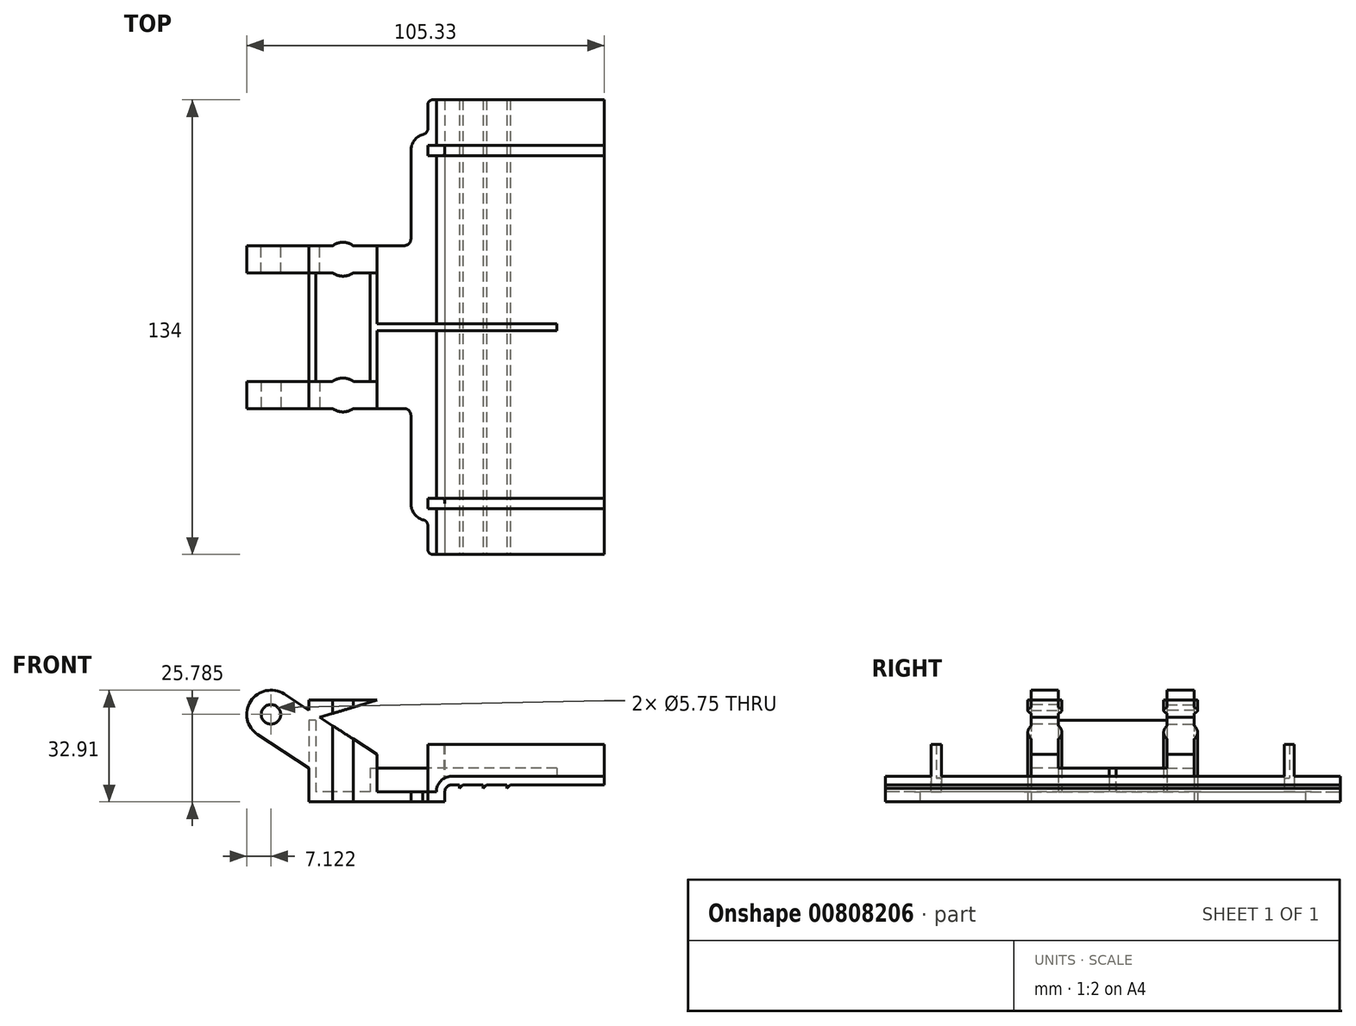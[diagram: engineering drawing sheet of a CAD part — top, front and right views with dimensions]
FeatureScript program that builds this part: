
annotation { "Feature Type Name" : "Feature", "Feature Type Description" : "" }
export const myFeature = defineFeature(function(context is Context, id is Id, definition is map)
    precondition{}
    {
        {
            var Q0;
            Q0=qCreatedBy(makeId("Top.planeOp"),FACE);
            var sketch = newSketch(context, id + "F0", { "sketchPlane" : qUnion([Q0])});
            skLineSegment(sketch, "E0", {"start": v(0, 0) * mm, "end": v(55, 0) * mm});
            skLineSegment(sketch, "E1", {"start": v(55, 0) * mm, "end": v(55, -1) * mm});
            skLineSegment(sketch, "E2", {"start": v(55, -1) * mm, "end": v(2, -1) * mm});
            skLineSegment(sketch, "E3", {"start": v(0, -1) * mm, "end": v(0, 0) * mm});
            skLineSegment(sketch, "E4", {"start": v(0, 0) * mm, "end": v(0, -16) * mm});
            skLineSegment(sketch, "E5", {"start": v(2, -24) * mm, "end": v(2, -1) * mm});
            skLineSegment(sketch, "E6", {"start": v(2, 0) * mm, "end": v(0, 0) * mm});
            skLineSegment(sketch, "E7.bottom", {"start": v(2, -24) * mm, "end": v(-5, -24) * mm});
            skLineSegment(sketch, "E7.top", {"start": v(0, -16) * mm, "end": v(-5, -16) * mm});
            skLineSegment(sketch, "E7.left", {"start": v(2, -24) * mm, "end": v(2, -16) * mm});
            skLineSegment(sketch, "E7.right", {"start": v(-18, -24) * mm, "end": v(-18, -16) * mm});
            skLineSegment(sketch, "E8", {"start": v(-18, -16) * mm, "end": v(-18, 0) * mm});
            skLineSegment(sketch, "E9", {"start": v(-18, 0) * mm, "end": v(-16, 0) * mm});
            skLineSegment(sketch, "E10", {"start": v(-16, 0) * mm, "end": v(-16, -16) * mm});
            skCircle(sketch, "E11", {"center": v(-8, -20) * mm, "radius": 5 * mm});
            skLineSegment(sketch, "E12", {"start": v(-16, 0) * mm, "end": v(0, 0) * mm});
            skLineSegment(sketch, "E13", {"start": v(2, -24) * mm, "end": v(10, -24) * mm});
            skLineSegment(sketch, "E14", {"start": v(12, -26) * mm, "end": v(12, -52) * mm});
            skLineSegment(sketch, "E15", {"start": v(17, -57) * mm, "end": v(22, -57) * mm});
            skLineSegment(sketch, "E16", {"start": v(22, -57) * mm, "end": v(22, -1) * mm});
            skLineSegment(sketch, "E17", {"start": v(0, -16) * mm, "end": v(2, -16) * mm});
            skCircle(sketch, "E18", {"center": v(17, -52) * mm, "radius": 5 * mm});
            skPoint(sketch, "E19.visualSharp", {"position": v(12, -57) * mm});
            skArc(sketch, "E19.filletArc", {"start": v(12, -52) * mm, "mid": v(13.46, -55.54) * mm, "end": v(17, -57) * mm});
            skLineSegment(sketch, "E20", {"start": v(2, -20) * mm, "end": v(-18, -20) * mm, "construction": true});
            skLineSegment(sketch, "E21.trimOffspring", {"start": v(-11, -16) * mm, "end": v(-18, -16) * mm});
            skLineSegment(sketch, "E22.trimOffspring", {"start": v(-11, -24) * mm, "end": v(-18, -24) * mm});
            skLineSegment(sketch, "E23.bottom", {"start": v(17, -53.5) * mm, "end": v(69, -53.5) * mm});
            skLineSegment(sketch, "E23.top", {"start": v(17, -50.5) * mm, "end": v(69, -50.5) * mm});
            skLineSegment(sketch, "E23.left", {"start": v(17, -53.5) * mm, "end": v(17, -50.5) * mm});
            skLineSegment(sketch, "E23.right", {"start": v(69, -53.5) * mm, "end": v(69, -50.5) * mm});
            skLineSegment(sketch, "E24", {"start": v(17, -52) * mm, "end": v(69, -52) * mm, "construction": true});
            skLineSegment(sketch, "E25.top", {"start": v(18.5, -67) * mm, "end": v(22, -67) * mm});
            skLineSegment(sketch, "E25.left", {"start": v(17, -58.5) * mm, "end": v(17, -65.5) * mm});
            skLineSegment(sketch, "E25.right", {"start": v(22, -57) * mm, "end": v(22, -67) * mm});
            skPoint(sketch, "E26.visualSharp", {"position": v(17, -67) * mm});
            skArc(sketch, "E26.filletArc", {"start": v(17, -65.5) * mm, "mid": v(17.44, -66.56) * mm, "end": v(18.5, -67) * mm});
            skPoint(sketch, "E27.visualSharp", {"position": v(12, -24) * mm});
            skArc(sketch, "E27.filletArc", {"start": v(12, -26) * mm, "mid": v(11.41, -24.59) * mm, "end": v(10, -24) * mm});
            skArc(sketch, "E28", {"start": v(17, -58.5) * mm, "mid": v(16.57, -57.36) * mm, "end": v(15.5, -56.77) * mm});
            skSolve(sketch);
        }
        {
            var Q0;
            Q0=makeQuery(id+"F0.imprint","IMPRINT",FACE,{"disambiguationData":[TD([[makeQuery(id+"F0.imprint","IMPRINT",EDGE,{"derivedFrom":sQuery(id+"F0.wireOp",EDGE,"E0")}),-1.0]])]});
            extrude(context, id + "F1", {"entities" : qUnion([Q0]), "depth" : 10 * mm, "offsetDistance" : 25 * mm});
        }
        {
            var Q0;
            {var subQ2=sQuery(id+"F0.wireOp",EDGE,"E7.bottom");Q0=makeQuery(id+"F0.imprint","IMPRINT",FACE,{"disambiguationData":[TD([[makeQuery(id+"F0.imprint","IMPRINT",EDGE,{"derivedFrom":subQ2}),-1.0]])]});}
            var Q1;
            {var subQ0=sQuery(id+"F0.wireOp",EDGE,"E11");var subQ1=makeQuery(id+"F0.imprint","INTERSECT",VERTEX,{"derivedFrom":[sQuery(id+"F0.wireOp",EDGE,"E7.top"),subQ0]});Q1=makeQuery(id+"F0.imprint","IMPRINT",FACE,{"disambiguationData":[TD([[makeQuery(id+"F0.imprint","IMPRINT",EDGE,{"disambiguationData":[TD([[subQ1,-1.0]])],"derivedFrom":subQ0}),1.0]])]});}
            var Q2;
            {var subQ1=sQuery(id+"F0.wireOp",EDGE,"E7.right");Q2=makeQuery(id+"F0.imprint","IMPRINT",FACE,{"disambiguationData":[TD([[makeQuery(id+"F0.imprint","IMPRINT",EDGE,{"derivedFrom":subQ1}),-1.0]])]});}
            extrude(context, id + "F2", {"entities" : qUnion([Q0, Q1, Q2]), "depth" : 30 * mm, "offsetDistance" : 25 * mm});
        }
        {
            var Q0;
            {var subQ0=sQuery(id+"F0.wireOp",EDGE,"E7.top");Q0=makeQuery(id+"F0.imprint","IMPRINT",FACE,{"disambiguationData":[TD([[makeQuery(id+"F0.imprint","IMPRINT",EDGE,{"derivedFrom":subQ0}),-1.0]])]});}
            var Q1;
            {var subQ1=sQuery(id+"F0.wireOp",EDGE,"E5");Q1=makeQuery(id+"F0.imprint","IMPRINT",FACE,{"disambiguationData":[TD([[makeQuery(id+"F0.imprint","IMPRINT",EDGE,{"derivedFrom":subQ1}),-1.0]])]});}
            var Q2;
            {var subQ0=sQuery(id+"F0.wireOp",EDGE,"E15");Q2=makeQuery(id+"F0.imprint","IMPRINT",FACE,{"disambiguationData":[TD([[makeQuery(id+"F0.imprint","IMPRINT",EDGE,{"derivedFrom":subQ0}),1.0]])]});}
            var Q3;
            Q3=makeQuery(id+"F0.imprint","IMPRINT",FACE,{"disambiguationData":[TD([[makeQuery(id+"F0.imprint","IMPRINT",EDGE,{"derivedFrom":sQuery(id+"F0.wireOp",EDGE,"E15")}),-1.0]])]});
            var Q4;
            {var subQ0=sQuery(id+"F0.wireOp",EDGE,"E23.left");Q4=makeQuery(id+"F0.imprint","IMPRINT",FACE,{"disambiguationData":[TD([[makeQuery(id+"F0.imprint","IMPRINT",EDGE,{"derivedFrom":subQ0}),-1.0]])]});}
            var Q5;
            {var subQ0=sQuery(id+"F0.wireOp",EDGE,"E23.left");Q5=makeQuery(id+"F0.imprint","IMPRINT",FACE,{"disambiguationData":[TD([[makeQuery(id+"F0.imprint","IMPRINT",EDGE,{"derivedFrom":subQ0}),1.0]])]});}
            var Q6;
            {var subQ0=sQuery(id+"F0.wireOp",EDGE,"E23.top");var subQ1=sQuery(id+"F0.wireOp",EDGE,"E16");var subQ2=makeQuery(id+"F0.imprint","INTERSECT",VERTEX,{"derivedFrom":[subQ1,subQ0]});Q6=makeQuery(id+"F0.imprint","IMPRINT",FACE,{"disambiguationData":[TD([[makeQuery(id+"F0.imprint","IMPRINT",EDGE,{"disambiguationData":[TD([[subQ2,1.0]])],"derivedFrom":subQ1}),1.0]])]});}
            var Q7;
            {var subQ0=sQuery(id+"F0.wireOp",EDGE,"E23.bottom");var subQ1=sQuery(id+"F0.wireOp",EDGE,"E16");var subQ2=makeQuery(id+"F0.imprint","INTERSECT",VERTEX,{"derivedFrom":[subQ1,subQ0]});Q7=makeQuery(id+"F0.imprint","IMPRINT",FACE,{"disambiguationData":[TD([[makeQuery(id+"F0.imprint","IMPRINT",EDGE,{"disambiguationData":[TD([[subQ2,-1.0]])],"derivedFrom":subQ1}),1.0]])]});}
            extrude(context, id + "F3", {"entities" : qUnion([Q0, Q1, Q2, Q3, Q4, Q5, Q6, Q7]), "depth" : 3 * mm, "offsetDistance" : 25 * mm});
        }
        {
            var Q0;
            {var subQ0=sQuery(id+"F0.wireOp",EDGE,"E18");var subQ1=makeQuery(id+"F0.imprint","INTERSECT",VERTEX,{"derivedFrom":[sQuery(id+"F0.wireOp",EDGE,"E14"),subQ0]});Q0=makeQuery(id+"F0.imprint","IMPRINT",FACE,{"disambiguationData":[TD([[makeQuery(id+"F0.imprint","IMPRINT",EDGE,{"disambiguationData":[TD([[subQ1,-1.0]])],"derivedFrom":subQ0}),1.0]])]});}
            var Q1;
            {var subQ0=sQuery(id+"F0.wireOp",EDGE,"E23.bottom");var subQ1=sQuery(id+"F0.wireOp",EDGE,"E16");var subQ2=makeQuery(id+"F0.imprint","INTERSECT",VERTEX,{"derivedFrom":[subQ1,subQ0]});Q1=makeQuery(id+"F0.imprint","IMPRINT",FACE,{"disambiguationData":[TD([[makeQuery(id+"F0.imprint","IMPRINT",EDGE,{"disambiguationData":[TD([[subQ2,-1.0]])],"derivedFrom":subQ1}),1.0]])]});}
            var Q2;
            {var subQ5=sQuery(id+"F0.wireOp",EDGE,"E23.right");Q2=makeQuery(id+"F0.imprint","IMPRINT",FACE,{"disambiguationData":[TD([[makeQuery(id+"F0.imprint","IMPRINT",EDGE,{"derivedFrom":subQ5}),1.0]])]});}
            var Q3;
            {var subQ5=sQuery(id+"F0.wireOp",EDGE,"E23.left");Q3=makeQuery(id+"F0.imprint","IMPRINT",FACE,{"disambiguationData":[TD([[makeQuery(id+"F0.imprint","IMPRINT",EDGE,{"derivedFrom":subQ5}),-1.0]])]});}
            extrude(context, id + "F4", {"entities" : qUnion([Q0, Q1, Q2, Q3]), "depth" : 17 * mm, "offsetDistance" : 25 * mm});
        }
        {
            var Q0;
            {var subQ0=sQuery(id+"F0.wireOp",EDGE,"E8");Q0=makeQuery(id+"F0.imprint","IMPRINT",FACE,{"disambiguationData":[TD([[makeQuery(id+"F0.imprint","IMPRINT",EDGE,{"derivedFrom":subQ0}),-1.0]])]});}
            extrude(context, id + "F5", {"entities" : qUnion([Q0]), "depth" : 24 * mm, "offsetDistance" : 25 * mm});
        }
        {
            var Q0;
            Q0=makeQuery(id+"F3.opExtrude","SWEPT_FACE",FACE,{"disambiguationData":[OSD([sQuery(id+"F0.wireOp",EDGE,"E25.top")])]});
            var sketch = newSketch(context, id + "F6", { "sketchPlane" : qUnion([Q0])});
            skLineSegment(sketch, "E29", {"start": v(22, 0) * mm, "end": v(22, 3) * mm});
            skLineSegment(sketch, "E30", {"start": v(24, 5) * mm, "end": v(69, 5) * mm});
            skPoint(sketch, "E31.visualSharp", {"position": v(22, 5) * mm});
            skArc(sketch, "E31.filletArc", {"start": v(24, 5) * mm, "mid": v(22.59, 4.41) * mm, "end": v(22, 3) * mm});
            skLineSegment(sketch, "E32", {"start": v(22, 0) * mm, "end": v(19.5, 0) * mm});
            skLineSegment(sketch, "E33", {"start": v(19.5, 0) * mm, "end": v(19.5, 3) * mm});
            skArc(sketch, "E34", {"start": v(19.5, 3) * mm, "mid": v(20.82, 6.18) * mm, "end": v(24, 7.5) * mm});
            skLineSegment(sketch, "E35", {"start": v(24, 7.5) * mm, "end": v(69, 7.5) * mm});
            skLineSegment(sketch, "E36", {"start": v(69, 7.5) * mm, "end": v(69, 5) * mm});
            skLineSegment(sketch, "E37", {"start": v(22, 0) * mm, "end": v(69, 0) * mm});
            skLineSegment(sketch, "E38", {"start": v(69, 0) * mm, "end": v(69, 5) * mm});
            skLineSegment(sketch, "E39", {"start": v(40.32, 5) * mm, "end": v(40.32, 4) * mm});
            skLineSegment(sketch, "E40", {"start": v(40.32, 4) * mm, "end": v(41.32, 5) * mm});
            skLineSegment(sketch, "E41", {"start": v(41.32, 5) * mm, "end": v(40.32, 5) * mm});
            skLineSegment(sketch, "E42", {"start": v(40.32, 5) * mm, "end": v(34.32, 5) * mm});
            skLineSegment(sketch, "E43", {"start": v(34.32, 5) * mm, "end": v(33.32, 4) * mm});
            skLineSegment(sketch, "E44", {"start": v(33.32, 4) * mm, "end": v(33.32, 5) * mm});
            skLineSegment(sketch, "E45", {"start": v(33.32, 5) * mm, "end": v(34.32, 5) * mm});
            skLineSegment(sketch, "E46", {"start": v(33.32, 5) * mm, "end": v(27.32, 5) * mm});
            skLineSegment(sketch, "E47", {"start": v(27.32, 5) * mm, "end": v(26.32, 4) * mm});
            skLineSegment(sketch, "E48", {"start": v(26.32, 4) * mm, "end": v(26.32, 5) * mm});
            skLineSegment(sketch, "E49", {"start": v(26.32, 5) * mm, "end": v(27.32, 5) * mm});
            skSolve(sketch);
        }
        {
            var Q0;
            {var subQ1=sQuery(id+"F6.wireOp",EDGE,"E31.filletArc");Q0=makeQuery(id+"F6.imprint","IMPRINT",FACE,{"disambiguationData":[TD([[makeQuery(id+"F6.imprint","IMPRINT",EDGE,{"derivedFrom":subQ1}),-1.0]])]});}
            var Q1;
            {var subQ0=sQuery(id+"F6.wireOp",EDGE,"E43");Q1=makeQuery(id+"F6.imprint","IMPRINT",FACE,{"disambiguationData":[TD([[makeQuery(id+"F6.imprint","IMPRINT",EDGE,{"derivedFrom":subQ0}),-1.0]])]});}
            var Q2;
            {var subQ2=sQuery(id+"F6.wireOp",EDGE,"E39");Q2=makeQuery(id+"F6.imprint","IMPRINT",FACE,{"disambiguationData":[TD([[makeQuery(id+"F6.imprint","IMPRINT",EDGE,{"derivedFrom":subQ2}),1.0]])]});}
            var Q3;
            {var subQ0=sQuery(id+"F6.wireOp",EDGE,"E47");Q3=makeQuery(id+"F6.imprint","IMPRINT",FACE,{"disambiguationData":[TD([[makeQuery(id+"F6.imprint","IMPRINT",EDGE,{"derivedFrom":subQ0}),-1.0]])]});}
            var Q4;
            Q4=makeQuery(id+"F1.opExtrude","SWEPT_FACE",FACE,{"disambiguationData":[OSD([sQuery(id+"F0.wireOp",EDGE,"E0"),sQuery(id+"F0.wireOp",EDGE,"E6")])]});
            extrude(context, id + "F7", {"entities" : qUnion([Q0, Q1, Q2, Q3]), "endBound" : BoundingType.UP_TO_SURFACE, "oppositeDirection" : true, "depth" : 59.56 * mm, "endBoundEntityFace" : qUnion([Q4]), "offsetDistance" : 25 * mm});
        }
        {
            var Q0;
            Q0=makeQuery(id+"F6.imprint","IMPRINT",FACE,{"disambiguationData":[TD([[makeQuery(id+"F6.imprint","IMPRINT",EDGE,{"derivedFrom":sQuery(id+"F6.wireOp",EDGE,"E29")}),1.0]])]});
            var Q1;
            Q1 = qSketchRegion(id + "F10", true);
            var Q2;
            Q2=makeQuery(id+"F1.opExtrude","SWEPT_FACE",FACE,{"disambiguationData":[OSD([sQuery(id+"F0.wireOp",EDGE,"E0"),sQuery(id+"F0.wireOp",EDGE,"E6")])]});
            extrude(context, id + "F8", {"entities" : qUnion([Q0, Q1]), "operationType" : NewBodyOperationType.REMOVE, "endBound" : BoundingType.UP_TO_SURFACE, "oppositeDirection" : true, "depth" : 25 * mm, "endBoundEntityFace" : qUnion([Q2]), "offsetDistance" : 25 * mm});
        }
        {
            var Q0;
            Q0=makeQuery(id+"F2.opExtrude","SWEPT_FACE",FACE,{"disambiguationData":[OSD([sQuery(id+"F0.wireOp",EDGE,"E22.trimOffspring")])]});
            var sketch = newSketch(context, id + "F9", { "sketchPlane" : qUnion([Q0])});
            skLineSegment(sketch, "E50", {"start": v(-18, 0) * mm, "end": v(-18, 10) * mm});
            skLineSegment(sketch, "E51", {"start": v(-18, 10) * mm, "end": v(-33.1, 19.8) * mm});
            skArc(sketch, "E52", {"start": v(-33.1, 19.8) * mm, "mid": v(-35.18, 29.67) * mm, "end": v(-25.32, 31.76) * mm});
            skLineSegment(sketch, "E53", {"start": v(-18, 0) * mm, "end": v(2, 0) * mm});
            skLineSegment(sketch, "E54", {"start": v(2, 0) * mm, "end": v(2, 14) * mm});
            skLineSegment(sketch, "E55", {"start": v(2, 14) * mm, "end": v(-25.32, 31.76) * mm});
            skCircle(sketch, "E56", {"center": v(-29.2, 25.79) * mm, "radius": 2.88 * mm});
            skLineSegment(sketch, "E57", {"start": v(2, 14) * mm, "end": v(2, 30) * mm});
            skPoint(sketch, "E57.endSnap0", {"position": v(-14.5, 30) * mm});
            skLineSegment(sketch, "E58", {"start": v(2, 30) * mm, "end": v(-14.8, 24.92) * mm});
            skLineSegment(sketch, "E59", {"start": v(-14.8, 24.92) * mm, "end": v(2, 14) * mm});
            skLineSegment(sketch, "E60", {"start": v(2, 30) * mm, "end": v(2, 14) * mm});
            skLineSegment(sketch, "E61", {"start": v(-18, 10) * mm, "end": v(-18, 27) * mm});
            skSolve(sketch);
        }
        {
            var Q0;
            {var subQ8=sQuery(id+"F9.wireOp",EDGE,"E51");Q0=makeQuery(id+"F9.imprint","IMPRINT",FACE,{"disambiguationData":[TD([[makeQuery(id+"F9.imprint","IMPRINT",EDGE,{"derivedFrom":subQ8}),-1.0]])]});}
            var sketch = newSketch(context, id + "F10", { "sketchPlane" : qUnion([Q0])});
            skSolve(sketch);
        }
        {
            var Q0;
            {var subQ8=sQuery(id+"F9.wireOp",EDGE,"E51");Q0=makeQuery(id+"F9.imprint","IMPRINT",FACE,{"disambiguationData":[TD([[makeQuery(id+"F9.imprint","IMPRINT",EDGE,{"derivedFrom":subQ8}),-1.0]])]});}
            var Q1;
            Q1 = qSketchRegion(id + "F10", true);
            var Q2;
            {var subQ4=sQuery(id+"F9.wireOp",EDGE,"E50");Q2=makeQuery(id+"F9.imprint","IMPRINT",FACE,{"disambiguationData":[TD([[makeQuery(id+"F9.imprint","IMPRINT",EDGE,{"derivedFrom":subQ4}),1.0]])]});}
            var Q3;
            {var subQ3=sQuery(id+"F9.wireOp",EDGE,"E54");Q3=makeQuery(id+"F9.imprint","IMPRINT",FACE,{"disambiguationData":[TD([[makeQuery(id+"F9.imprint","IMPRINT",EDGE,{"derivedFrom":subQ3}),1.0]])]});}
            var Q4;
            Q4=makeQuery(id+"F2.opExtrude","SWEPT_FACE",FACE,{"disambiguationData":[OSD([sQuery(id+"F0.wireOp",EDGE,"E21.trimOffspring")])]});
            var Q5;
            Q5=makeQuery(id+"F2.opExtrude","SWEPT_BODY",BODY,{"disambiguationData":[OSD([sQuery(id+"F0.wireOp",EDGE,"E7.bottom"),sQuery(id+"F0.wireOp",EDGE,"E7.top"),sQuery(id+"F0.wireOp",EDGE,"E7.left"),sQuery(id+"F0.wireOp",EDGE,"E7.right"),sQuery(id+"F0.wireOp",EDGE,"E11"),sQuery(id+"F0.wireOp",EDGE,"E17"),sQuery(id+"F0.wireOp",EDGE,"E21.trimOffspring"),sQuery(id+"F0.wireOp",EDGE,"E22.trimOffspring")])]});
            extrude(context, id + "F11", {"entities" : qUnion([Q0, Q1, Q2, Q3]), "operationType" : NewBodyOperationType.ADD, "endBound" : BoundingType.UP_TO_SURFACE, "oppositeDirection" : true, "depth" : 7.6 * mm, "endBoundEntityFace" : qUnion([Q4]), "endBoundEntityBody" : qUnion([Q5]), "offsetDistance" : 25 * mm});
        }
        {
            var Q0;
            {var subQ5=sQuery(id+"F9.wireOp",EDGE,"E57");Q0=makeQuery(id+"F9.imprint","IMPRINT",FACE,{"disambiguationData":[TD([[makeQuery(id+"F9.imprint","IMPRINT",EDGE,{"derivedFrom":subQ5}),1.0]])]});}
            var Q1;
            {var subQ0=sQuery(id+"F9.wireOp",EDGE,"E55");var subQ1=sQuery(id+"F0.wireOp",EDGE,"E22.trimOffspring");var subQ4=makeQuery(id+"F2.opExtrude","CAP_EDGE",EDGE,{"disambiguationData":[OSD([subQ1])],"isStart":false});var subQ5=makeQuery(id+"F9.imprint","INTERSECT",VERTEX,{"derivedFrom":[subQ4,subQ0]});Q1=makeQuery(id+"F9.imprint","IMPRINT",FACE,{"disambiguationData":[TD([[makeQuery(id+"F9.imprint","IMPRINT",EDGE,{"disambiguationData":[TD([[subQ5,1.0]])],"derivedFrom":subQ0}),-1.0]])]});}
            extrude(context, id + "F12", {"entities" : qUnion([Q0, Q1]), "operationType" : NewBodyOperationType.REMOVE, "oppositeDirection" : true, "depth" : 25 * mm, "offsetDistance" : 25 * mm, "hasSecondDirection" : true, "secondDirectionOppositeDirection" : false, "secondDirectionDepth" : 25 * mm});
        }
        {
            var Q0;
            Q0=makeQuery(id+"F2.opExtrude","SWEPT_BODY",BODY,{"disambiguationData":[OSD([sQuery(id+"F0.wireOp",EDGE,"E7.bottom"),sQuery(id+"F0.wireOp",EDGE,"E7.top"),sQuery(id+"F0.wireOp",EDGE,"E7.left"),sQuery(id+"F0.wireOp",EDGE,"E7.right"),sQuery(id+"F0.wireOp",EDGE,"E11"),sQuery(id+"F0.wireOp",EDGE,"E17"),sQuery(id+"F0.wireOp",EDGE,"E21.trimOffspring"),sQuery(id+"F0.wireOp",EDGE,"E22.trimOffspring")])]});
            var Q1;
            Q1=makeQuery(id+"F4.opExtrude","SWEPT_BODY",BODY,{"disambiguationData":[OSD([sQuery(id+"F0.wireOp",EDGE,"E16"),sQuery(id+"F0.wireOp",EDGE,"E18"),sQuery(id+"F0.wireOp",EDGE,"E23.bottom"),sQuery(id+"F0.wireOp",EDGE,"E23.top"),sQuery(id+"F0.wireOp",EDGE,"E23.right")])]});
            var Q2;
            Q2=makeQuery(id+"F3.opExtrude","SWEPT_BODY",BODY,{"disambiguationData":[OSD([sQuery(id+"F0.wireOp",EDGE,"E4"),sQuery(id+"F0.wireOp",EDGE,"E7.top"),sQuery(id+"F0.wireOp",EDGE,"E10"),sQuery(id+"F0.wireOp",EDGE,"E11"),sQuery(id+"F0.wireOp",EDGE,"E12"),sQuery(id+"F0.wireOp",EDGE,"E21.trimOffspring")])]});
            var Q3;
            Q3=makeQuery(id+"F1.opExtrude","SWEPT_BODY",BODY,{"disambiguationData":[OSD([sQuery(id+"F0.wireOp",EDGE,"E0"),sQuery(id+"F0.wireOp",EDGE,"E1"),sQuery(id+"F0.wireOp",EDGE,"E2"),sQuery(id+"F0.wireOp",EDGE,"E4"),sQuery(id+"F0.wireOp",EDGE,"E5"),sQuery(id+"F0.wireOp",EDGE,"E6"),sQuery(id+"F0.wireOp",EDGE,"E17")])]});
            var Q4;
            Q4=makeQuery(id+"F3.opExtrude","SWEPT_BODY",BODY,{"disambiguationData":[OSD([sQuery(id+"F0.wireOp",EDGE,"E2"),sQuery(id+"F0.wireOp",EDGE,"E5"),sQuery(id+"F0.wireOp",EDGE,"E7.left"),sQuery(id+"F0.wireOp",EDGE,"E13"),sQuery(id+"F0.wireOp",EDGE,"E14"),sQuery(id+"F0.wireOp",EDGE,"E16"),sQuery(id+"F0.wireOp",EDGE,"E18"),sQuery(id+"F0.wireOp",EDGE,"E25.top"),sQuery(id+"F0.wireOp",EDGE,"E25.left"),sQuery(id+"F0.wireOp",EDGE,"E25.right"),sQuery(id+"F0.wireOp",EDGE,"E26.filletArc"),sQuery(id+"F0.wireOp",EDGE,"E27.filletArc")])]});
            var Q5;
            Q5=makeQuery(id+"F7.opExtrude","SWEPT_BODY",BODY,{"disambiguationData":[OSD([sQuery(id+"F0.wireOp",EDGE,"E25.top"),sQuery(id+"F6.wireOp",EDGE,"E30"),sQuery(id+"F6.wireOp",EDGE,"E31.filletArc"),sQuery(id+"F6.wireOp",EDGE,"E34"),sQuery(id+"F6.wireOp",EDGE,"E35"),sQuery(id+"F6.wireOp",EDGE,"E36"),sQuery(id+"F6.wireOp",EDGE,"E39"),sQuery(id+"F6.wireOp",EDGE,"E40"),sQuery(id+"F6.wireOp",EDGE,"E43"),sQuery(id+"F6.wireOp",EDGE,"E44"),sQuery(id+"F6.wireOp",EDGE,"E46"),sQuery(id+"F6.wireOp",EDGE,"E47"),sQuery(id+"F6.wireOp",EDGE,"E48"),sQuery(id+"F6.wireOp",EDGE,"E42")])]});
            var Q6;
            Q6=makeQuery(id+"F5.opExtrude","SWEPT_BODY",BODY,{"disambiguationData":[OSD([sQuery(id+"F0.wireOp",EDGE,"E8"),sQuery(id+"F0.wireOp",EDGE,"E9"),sQuery(id+"F0.wireOp",EDGE,"E10"),sQuery(id+"F0.wireOp",EDGE,"E21.trimOffspring")])]});
            var Q7;
            Q7=makeQuery(id+"F3.opExtrude","SWEPT_FACE",FACE,{"disambiguationData":[OSD([sQuery(id+"F0.wireOp",EDGE,"E12")])]});
            mirror(context, id + "F13", {"operationType" : NewBodyOperationType.ADD, "entities" : qUnion([Q0, Q1, Q2, Q3, Q4, Q5, Q6]), "mirrorPlane" : qUnion([Q7])});
        }
    });
